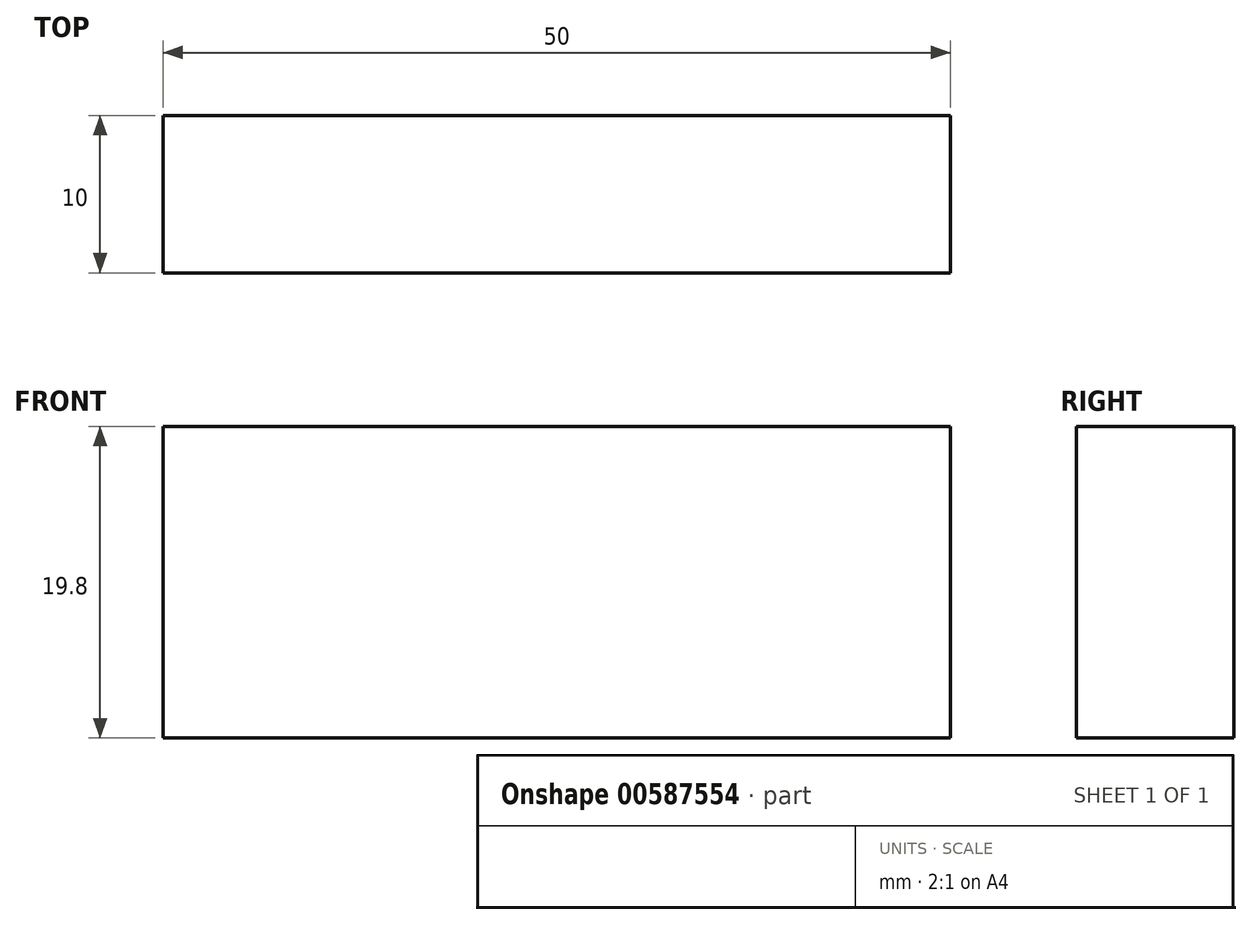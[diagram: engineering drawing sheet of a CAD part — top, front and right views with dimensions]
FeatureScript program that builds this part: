
annotation { "Feature Type Name" : "Feature", "Feature Type Description" : "" }
export const myFeature = defineFeature(function(context is Context, id is Id, definition is map)
    precondition{}
    {
        {
            var Q0;
            Q0=qCreatedBy(makeId("Front.planeOp"),FACE);
            var sketch = newSketch(context, id + "F0", { "sketchPlane" : qUnion([Q0])});
            skLineSegment(sketch, "E0.bottom", {"start": v(-50, 26.27) * mm, "end": v(0, 26.27) * mm});
            skLineSegment(sketch, "E0.top", {"start": v(-50, 6.47) * mm, "end": v(0, 6.47) * mm});
            skLineSegment(sketch, "E0.left", {"start": v(-50, 26.27) * mm, "end": v(-50, 6.47) * mm});
            skLineSegment(sketch, "E0.right", {"start": v(0, 26.27) * mm, "end": v(0, 6.47) * mm});
            skSolve(sketch);
        }
        {
            var Q0;
            Q0 = qSketchRegion(id + "F0", true);
            extrude(context, id + "F1", {"entities" : qUnion([Q0]), "depth" : 10 * mm, "offsetDistance" : 25 * mm});
        }
    });
